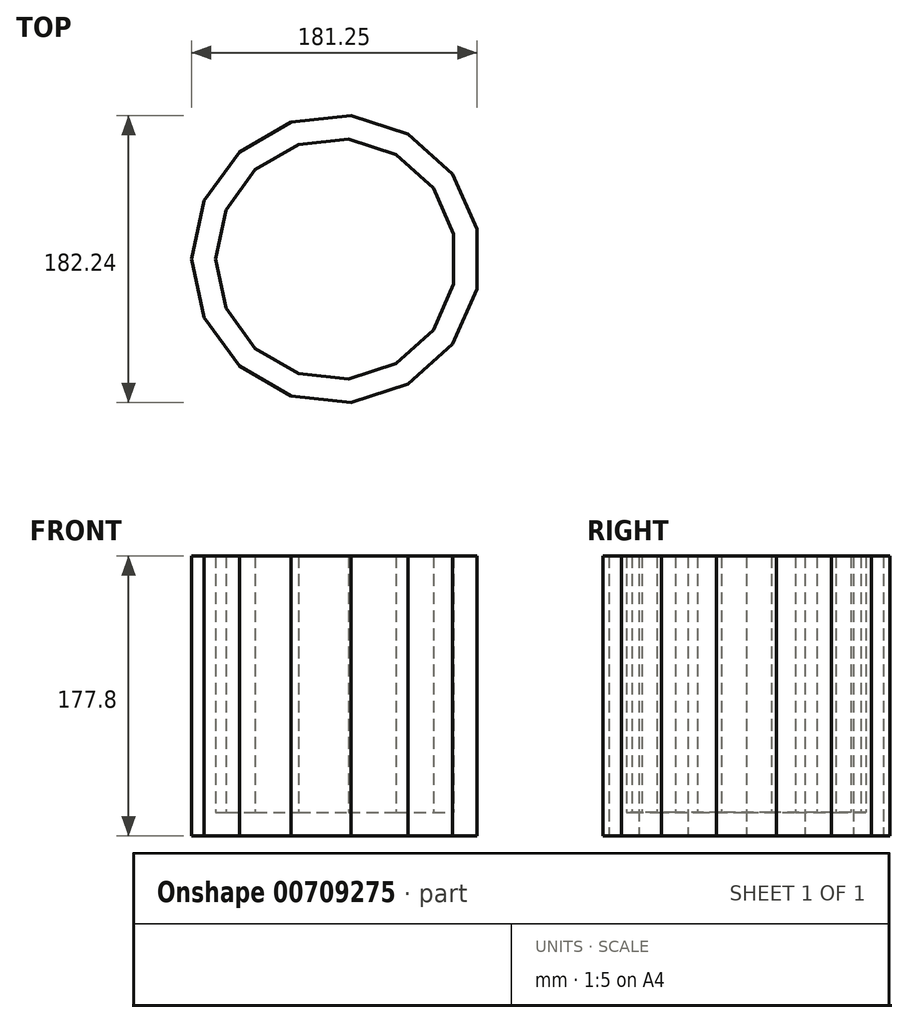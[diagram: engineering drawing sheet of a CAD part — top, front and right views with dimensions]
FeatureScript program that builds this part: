
annotation { "Feature Type Name" : "Feature", "Feature Type Description" : "" }
export const myFeature = defineFeature(function(context is Context, id is Id, definition is map)
    precondition{}
    {
        {
            var Q0;
            Q0=qCreatedBy(makeId("Top.planeOp"),FACE);
            var sketch = newSketch(context, id + "F0", { "sketchPlane" : qUnion([Q0])});
            skCircle(sketch, "E0.cCircle", {"center": v(0, 0) * mm, "radius": 89.62 * mm, "construction": true});
            skLineSegment(sketch, "E0.0", {"start": v(89.62, 19.05) * mm, "end": v(89.62, -19.05) * mm});
            skLineSegment(sketch, "E0.1", {"start": v(89.62, -19.05) * mm, "end": v(74.13, -53.86) * mm});
            skLineSegment(sketch, "E0.2", {"start": v(74.13, -53.86) * mm, "end": v(45.81, -79.35) * mm});
            skLineSegment(sketch, "E0.3", {"start": v(45.81, -79.35) * mm, "end": v(9.58, -91.12) * mm});
            skLineSegment(sketch, "E0.4", {"start": v(9.58, -91.12) * mm, "end": v(-28.31, -87.14) * mm});
            skLineSegment(sketch, "E0.5", {"start": v(-28.31, -87.14) * mm, "end": v(-61.3, -68.1) * mm});
            skLineSegment(sketch, "E0.6", {"start": v(-61.3, -68.1) * mm, "end": v(-83.7, -37.27) * mm});
            skLineSegment(sketch, "E0.7", {"start": v(-83.7, -37.27) * mm, "end": v(-91.63, 0) * mm});
            skLineSegment(sketch, "E0.8", {"start": v(-91.63, 0) * mm, "end": v(-83.7, 37.27) * mm});
            skLineSegment(sketch, "E0.9", {"start": v(-83.7, 37.27) * mm, "end": v(-61.3, 68.1) * mm});
            skLineSegment(sketch, "E0.10", {"start": v(-61.3, 68.1) * mm, "end": v(-28.31, 87.14) * mm});
            skLineSegment(sketch, "E0.11", {"start": v(-28.31, 87.14) * mm, "end": v(9.58, 91.12) * mm});
            skLineSegment(sketch, "E0.12", {"start": v(9.58, 91.12) * mm, "end": v(45.81, 79.35) * mm});
            skLineSegment(sketch, "E0.13", {"start": v(45.81, 79.35) * mm, "end": v(74.13, 53.86) * mm});
            skLineSegment(sketch, "E0.14", {"start": v(74.13, 53.86) * mm, "end": v(89.62, 19.05) * mm});
            skPoint(sketch, "E0.0.midPoint", {"position": v(89.62, 0) * mm});
            skSolve(sketch);
        }
        {
            var Q0;
            Q0 = qSketchRegion(id + "F0", true);
            extrude(context, id + "F1", {"entities" : qUnion([Q0]), "depth" : 177.8 * mm, "offsetDistance" : 25.4 * mm});
        }
        {
            var Q0;
            Q0=makeQuery(id+"F1.opExtrude","CAP_FACE",FACE,{"disambiguationData":[OSD([sQuery(id+"F0.wireOp",EDGE,"E0.0"),sQuery(id+"F0.wireOp",EDGE,"E0.1"),sQuery(id+"F0.wireOp",EDGE,"E0.2"),sQuery(id+"F0.wireOp",EDGE,"E0.3"),sQuery(id+"F0.wireOp",EDGE,"E0.4"),sQuery(id+"F0.wireOp",EDGE,"E0.5"),sQuery(id+"F0.wireOp",EDGE,"E0.6"),sQuery(id+"F0.wireOp",EDGE,"E0.7"),sQuery(id+"F0.wireOp",EDGE,"E0.8"),sQuery(id+"F0.wireOp",EDGE,"E0.9"),sQuery(id+"F0.wireOp",EDGE,"E0.10"),sQuery(id+"F0.wireOp",EDGE,"E0.11"),sQuery(id+"F0.wireOp",EDGE,"E0.12"),sQuery(id+"F0.wireOp",EDGE,"E0.13"),sQuery(id+"F0.wireOp",EDGE,"E0.14")])],"isStart":false});
            shell(context, id + "F2", {"entities" : qUnion([Q0]), "thickness" : 14.82 * mm});
        }
    });
